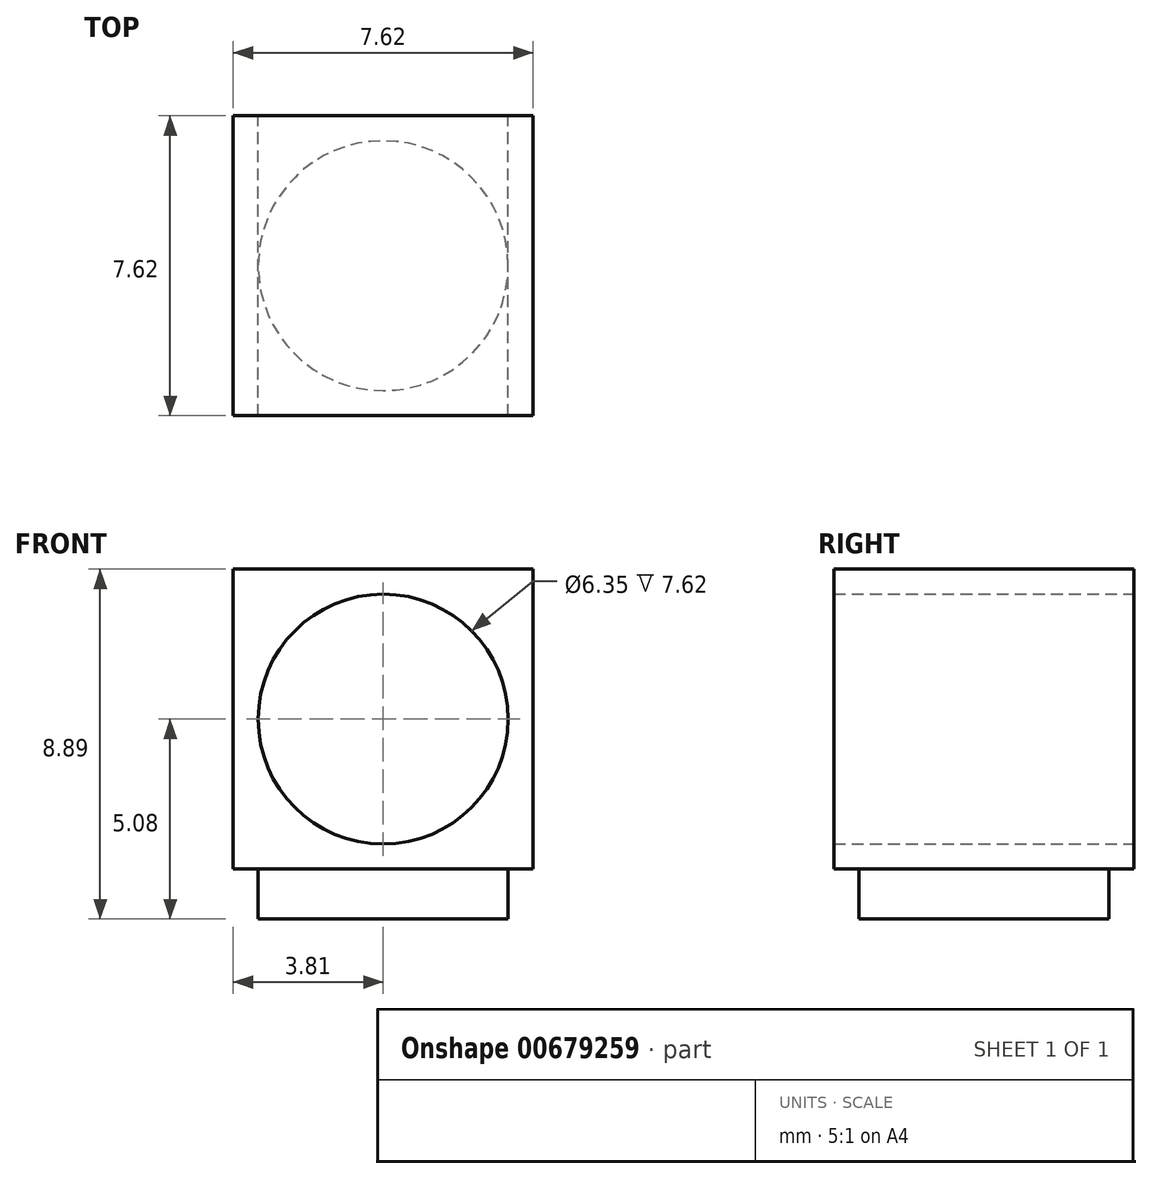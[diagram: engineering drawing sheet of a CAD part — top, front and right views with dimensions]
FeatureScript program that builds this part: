
annotation { "Feature Type Name" : "Feature", "Feature Type Description" : "" }
export const myFeature = defineFeature(function(context is Context, id is Id, definition is map)
    precondition{}
    {
        {
            var Q0;
            Q0=qCreatedBy(makeId("Front.planeOp"),FACE);
            var sketch = newSketch(context, id + "F0", { "sketchPlane" : qUnion([Q0])});
            skLineSegment(sketch, "E0.bottom", {"start": v(3.8, 3.81) * mm, "end": v(-3.81, 3.81) * mm});
            skLineSegment(sketch, "E0.top", {"start": v(3.81, -3.8) * mm, "end": v(-3.81, -3.8) * mm});
            skLineSegment(sketch, "E0.left", {"start": v(3.8, 3.81) * mm, "end": v(3.8, -3.8) * mm});
            skLineSegment(sketch, "E0.right", {"start": v(-3.81, 3.81) * mm, "end": v(-3.81, -3.8) * mm});
            skPoint(sketch, "E0.middle", {"position": v(0, 0) * mm});
            skCircle(sketch, "E1", {"center": v(0, 0) * mm, "radius": 3.18 * mm});
            skSolve(sketch);
        }
        {
            var Q0;
            Q0=qSketchRegion(id+"F0",true);
            extrude(context, id + "F1", {"entities" : qUnion([Q0]), "depth" : 7.62 * mm, "offsetDistance" : 25.4 * mm});
        }
        {
            var Q0;
            Q0=makeQuery(id+"F1.opExtrude","SWEPT_FACE",FACE,{"disambiguationData":[OSD([sQuery(id+"F0.wireOp",EDGE,"E0.top")])]});
            var sketch = newSketch(context, id + "F2", { "sketchPlane" : qUnion([Q0])});
            skCircle(sketch, "E2", {"center": v(0, 3.81) * mm, "radius": 3.18 * mm});
            skPoint(sketch, "E2.centerSnap0", {"position": v(3.8, 3.81) * mm});
            skSolve(sketch);
        }
        {
            var Q0;
            Q0=qSketchRegion(id+"F2",true);
            extrude(context, id + "F3", {"entities" : qUnion([Q0]), "operationType" : NewBodyOperationType.ADD, "depth" : 1.27 * mm, "offsetDistance" : 25.4 * mm});
        }
    });
